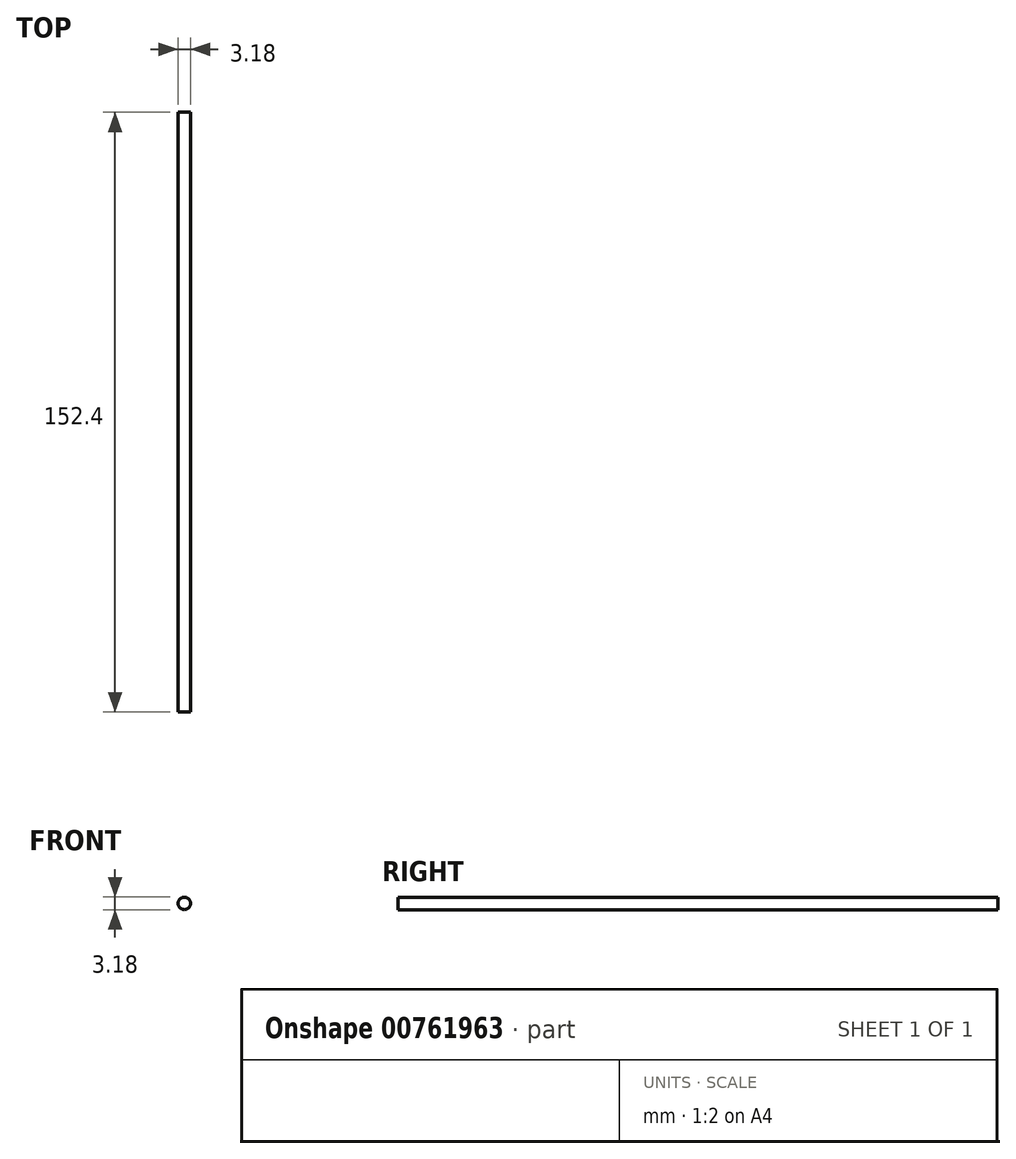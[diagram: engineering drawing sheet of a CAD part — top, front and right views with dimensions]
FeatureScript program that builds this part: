
annotation { "Feature Type Name" : "Feature", "Feature Type Description" : "" }
export const myFeature = defineFeature(function(context is Context, id is Id, definition is map)
    precondition{}
    {
        {
            var Q0;
            Q0=qCreatedBy(makeId("Front.planeOp"),FACE);
            var sketch = newSketch(context, id + "F0", { "sketchPlane" : qUnion([Q0])});
            skCircle(sketch, "E0", {"center": v(0, 0) * mm, "radius": 1.59 * mm});
            skSolve(sketch);
        }
        {
            var Q0;
            Q0=makeQuery(id+"F0.imprint","IMPRINT",FACE,{"disambiguationData":[TD([[makeQuery(id+"F0.imprint","IMPRINT",EDGE,{"derivedFrom":sQuery(id+"F0.wireOp",EDGE,"E0")}),1.0]])]});
            extrude(context, id + "F1", {"entities" : qUnion([Q0]), "oppositeDirection" : true, "depth" : 152.4 * mm, "offsetDistance" : 25.4 * mm});
        }
    });
